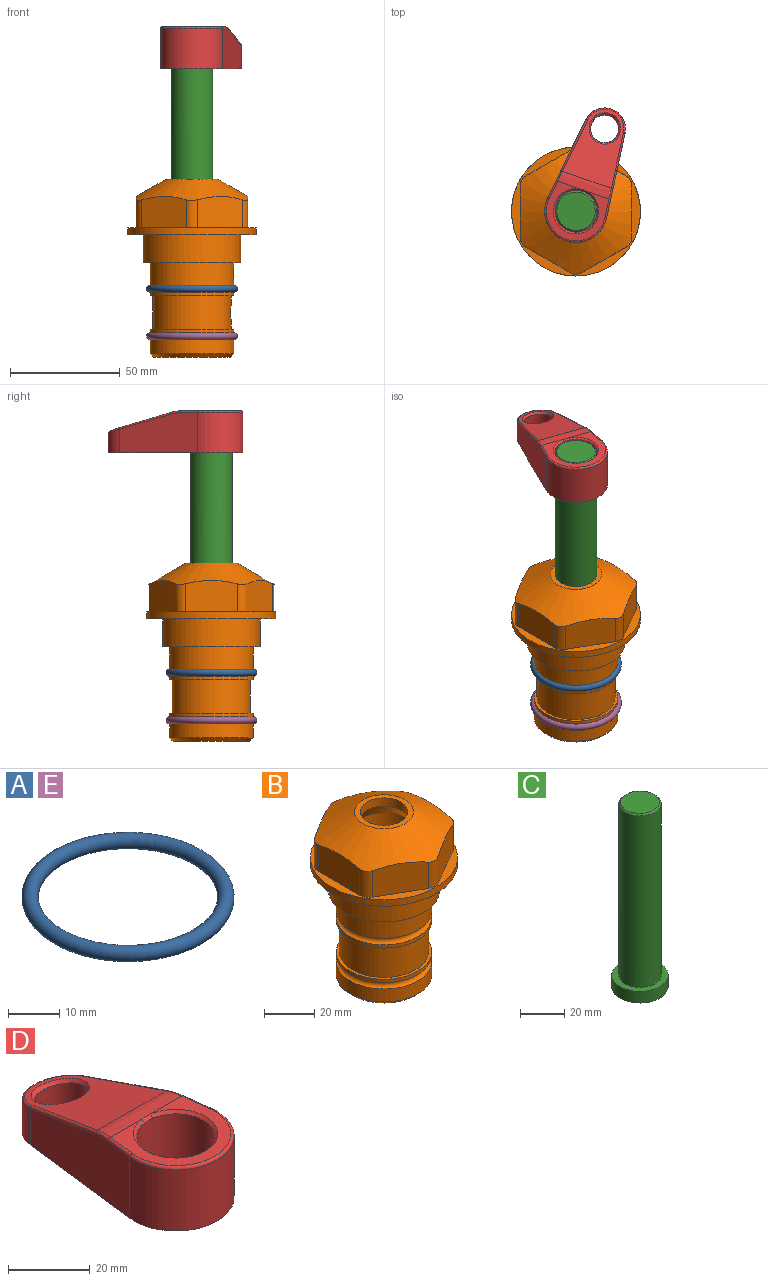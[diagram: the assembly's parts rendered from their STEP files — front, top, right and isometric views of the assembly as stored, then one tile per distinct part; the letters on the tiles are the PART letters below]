
ASSEMBLY  parts=5 mates=3
PART A: 1 faces, bbox 44.7x44.7x3.2 mm
  f0: torus R=19.05mm, axis (0,0,1), area 1193.9mm2
PART B: 36 faces, bbox 58.7x58.7x81 mm
  f0: cylinder r=17.78mm len=35.56mm, axis (0,0,1), area 1670.8mm2, adj f23,f24,f31
  f1: cylinder r=19.05mm len=38.1mm, axis (0,0,1), area 1191.9mm2, adj f26,f27,f30
  f2: plane 58.66x58.66mm, normal (0,0,-1), area 1150.6mm2, adj f3,f28
  f3: cylinder r=29.33mm len=58.66mm, axis (0,0,-1), area 585.1mm2, adj f2,f4
  f4: plane 58.66x58.66mm, normal (0,0,1), area 475.9mm2, adj f3,f5,f6,f7,f8,f9,f10,f11
  f5: plane 20.32x14.34mm, normal (-0.5,0.87,0), area 324.4mm2, adj f4,f15,f16,f17
  f6: plane 20.32x14.34mm, normal (0.5,0.87,0), area 324.4mm2, adj f4,f14,f15,f17
  f7: plane 23.48x14.34mm, normal (1,0,0), area 324.4mm2, adj f4,f13,f14,f17
  f8: plane 20.32x14.34mm, normal (0.5,-0.87,0), area 324.4mm2, adj f4,f12,f13,f17
  f9: plane 20.32x14.34mm, normal (-0.5,-0.87,0), area 324.4mm2, adj f4,f11,f12,f17
  f10: plane 23.48x14.34mm, normal (-1,0,0), area 324.4mm2, adj f4,f11,f16,f17
  f11: cylinder r=5.08mm len=12.85mm, axis (0,0,-1), area 67.2mm2, adj f4,f9,f10,f17
  f12: cylinder r=5.08mm len=12.85mm, axis (0,0,-1), area 67.2mm2, adj f4,f8,f9,f17
  f13: cylinder r=5.08mm len=12.85mm, axis (0,0,-1), area 67.2mm2, adj f4,f7,f8,f17
  f14: cylinder r=5.08mm len=12.85mm, axis (0,0,-1), area 67.2mm2, adj f4,f6,f7,f17
  f15: cylinder r=5.08mm len=12.85mm, axis (0,0,-1), area 67.2mm2, adj f4,f5,f6,f17
  f16: cylinder r=5.08mm len=12.85mm, axis (0,0,-1), area 67.2mm2, adj f4,f5,f10,f17
  f17: cone r=11.73mm half-angle=60deg, axis (0,0,-1), area 2071.8mm2, adj f5,f6,f7,f8,f9,f10,f11,f12
  f18: plane 23.46x23.46mm, normal (0,0,1), area 147.4mm2, adj f17,f35
  f19: plane 34.93x34.93mm, normal (0,0,-1), area 958mm2, adj f29
  f20: cylinder r=19.05mm len=38.1mm, axis (0,0,1), area 760.1mm2, adj f21,f29
  f21: torus R=19.05mm, axis (0,0,1), area 565.3mm2, adj f20,f22
  f22: cylinder r=19.05mm len=38.1mm, axis (0,0,1), area 190mm2, adj f21,f23
  f23: plane 38.1x38.1mm, normal (0,0,1), area 146.9mm2, adj f0,f22
  f24: plane 38.1x38.1mm, normal (0,0,-1), area 146.9mm2, adj f0,f25
  f25: cylinder r=19.05mm len=38.1mm, axis (0,0,1), area 190mm2, adj f24,f26
  f26: torus R=19.05mm, axis (0,0,1), area 565.3mm2, adj f1,f25
  f27: plane 44.45x44.45mm, normal (0,0,-1), area 411.7mm2, adj f1,f28
  f28: cylinder r=22.23mm len=44.45mm, axis (0,0,1), area 1773.5mm2, adj f2,f27
  f29: cone r=19.05mm half-angle=45deg, axis (0,0,1), area 257.5mm2, adj f19,f20
  f30: cylinder r=3.17mm len=6.75mm, axis (-1,0,0), area 128mm2, adj f1,f33
  f31: cylinder r=3.17mm len=6.35mm, axis (-1,0,0), area 102.5mm2, adj f0,f33
  f32: plane 25.4x25.4mm, normal (0,0,1), area 506.7mm2, adj f33
  f33: cylinder r=12.7mm len=66.42mm, axis (0,0,-1), area 5236.2mm2, adj f30,f31,f32,f34
  f34: cone r=9.53mm half-angle=30deg, axis (0,0,-1), area 443.4mm2, adj f33,f35
  f35: cylinder r=9.53mm len=19.05mm, axis (0,0,-1), area 240.9mm2, adj f18,f34
PART C: 6 faces, bbox 25.4x25.4x101.6 mm
  f0: plane 17.46x17.46mm, normal (0,0,1), area 239.5mm2, adj f5
  f1: plane 25.4x25.4mm, normal (0,0,-1), area 506.7mm2, adj f2
  f2: cylinder r=12.7mm len=25.4mm, axis (0,0,1), area 506.7mm2, adj f1,f3
  f3: plane 25.4x25.4mm, normal (0,0,1), area 221.7mm2, adj f2,f4
  f4: cylinder r=9.53mm len=94.46mm, axis (0,0,1), area 5653mm2, adj f3,f5
  f5: cone r=8.73mm half-angle=45deg, axis (0,0,-1), area 64.4mm2, adj f0,f4
PART D: 31 faces, bbox 31.7x65.5x19.8 mm
  f0: plane 39.12x18.26mm, normal (0.99,0.12,0), area 612.2mm2, adj f1,f4,f7,f11,f13,f15
  f1: cylinder r=9.53mm len=18.91mm, axis (0,0,-1), area 296.1mm2, adj f0,f2,f7,f17
  f2: plane 39.12x18.26mm, normal (-0.99,0.12,0), area 612.2mm2, adj f1,f4,f7,f12,f14,f16
  f3: cylinder r=6.35mm len=12.7mm, axis (0,0,-1), area 362.4mm2, adj f7,f18
  f4: cylinder r=14.29mm len=28.58mm, axis (0,0,-1), area 882.2mm2, adj f0,f2,f7,f10
  f5: cylinder r=9.53mm len=19.05mm, axis (0,0,-1), area 1092.6mm2, adj f7,f19,f20
  f6: plane 26.99x23.69mm, normal (0,0,1), area 216.2mm2, adj f9,f10,f11,f12,f19
  f7: plane 63.5x28.58mm, normal (0,0,-1), area 661.8mm2, adj f0,f1,f2,f3,f4,f5,f22,f23
  f8: plane 33.52x23.6mm, normal (0,0.26,0.97), area 486mm2, adj f9,f15,f16,f17,f18
  f9: cylinder r=19.05mm len=24.72mm, axis (1,0,0), area 120.4mm2, adj f6,f8,f13,f14,f20
  f10: torus R=13.49mm, axis (0,0,1), area 59mm2, adj f4,f6,f11,f12
  f11: cylinder r=0.79mm len=8.67mm, axis (0.12,-0.99,0), area 10.8mm2, adj f0,f6,f10,f13
  f12: cylinder r=0.79mm len=8.67mm, axis (0.12,0.99,0), area 10.8mm2, adj f2,f6,f10,f14
  f13: bspline ~4.95x1.42mm, area 6.1mm2, adj f0,f9,f11,f15
  f14: bspline ~4.95x1.42mm, area 6.1mm2, adj f2,f9,f12,f16
  f15: cylinder r=0.79mm len=25.95mm, axis (0.12,-0.96,0.26), area 32.9mm2, adj f0,f8,f13,f17
  f16: cylinder r=0.79mm len=25.95mm, axis (0.12,0.96,-0.26), area 32.9mm2, adj f2,f8,f14,f17
  f17: bspline ~18.91x8.38mm, area 30mm2, adj f1,f8,f15,f16
  f18: bspline ~14.29x14.29mm, area 48.3mm2, adj f3,f8
  f19: cone r=9.53mm half-angle=45deg, axis (0,0,1), area 66.5mm2, adj f5,f6,f20
  f20: bspline ~3.22x0.96mm, area 3.5mm2, adj f5,f9,f19
  f21: plane 2.75x2.72mm, normal (0,0,-1), area 2.9mm2, adj f23,f25,f28
  f22: plane 23.05x15.88mm, normal (-0.99,-0.12,0), area 323.6mm2, adj f7,f25,f26,f27,f28,f29
  f23: plane 23.05x15.88mm, normal (0.99,-0.12,0), area 323.6mm2, adj f7,f21,f25,f27,f28,f30
  f24: cylinder r=9.53mm len=10.69mm, axis (0,0,-1), area 114.7mm2, adj f7,f27,f29,f30
  f25: cylinder r=12.7mm len=20.59mm, axis (0,0,-1), area 381.1mm2, adj f7,f21,f22,f23,f26,f28
  f26: plane 2.75x2.72mm, normal (0,0,-1), area 2.9mm2, adj f22,f25,f28
  f27: plane 19.72x18.37mm, normal (0,-0.26,-0.97), area 291.8mm2, adj f22,f23,f24,f28,f29,f30
  f28: cylinder r=15.88mm len=19.92mm, axis (1,0,0), area 54.8mm2, adj f21,f22,f23,f25,f26,f27
  f29: cylinder r=1.59mm len=11mm, axis (0,0,-1), area 34.7mm2, adj f7,f22,f24,f27
  f30: cylinder r=1.59mm len=11mm, axis (0,0,-1), area 34.7mm2, adj f7,f23,f24,f27
PART E: same geometry as A
PLACE A at identity
PLACE B at identity fixed
PLACE C rot(axis=(0,0,-1),19.2deg) t=(0,0,30.41)mm
PLACE D rot(axis=(0,0,-1),19.2deg) t=(0,0,31.21)mm
PLACE E t=(0,0,-21.59)mm
MATE fastened C.f2 <-> D.f4  axis (0,0,1) through (0,0,93.91)mm
MATE fastened B.f0 <-> E.f0  axis (0,0,1) through (0,0,-46.1)mm
MATE cylindrical C.f2 <-> B.f0  axis (0,0,-1) through (0,0,-7.69)mm
